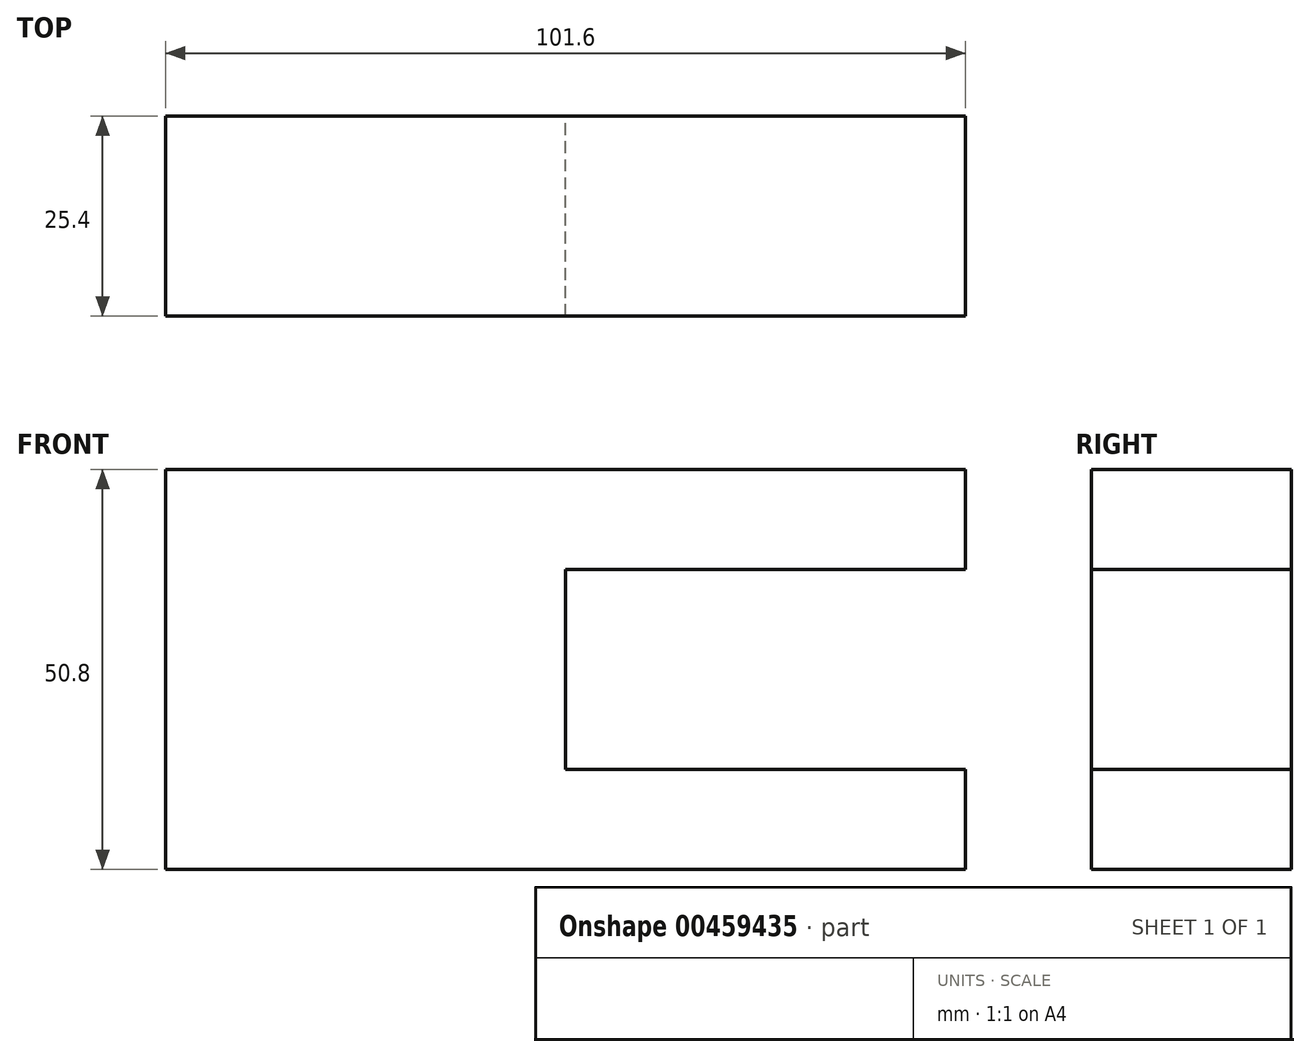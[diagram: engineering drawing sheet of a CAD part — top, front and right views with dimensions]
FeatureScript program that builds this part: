
annotation { "Feature Type Name" : "Feature", "Feature Type Description" : "" }
export const myFeature = defineFeature(function(context is Context, id is Id, definition is map)
    precondition{}
    {
        {
            var Q0;
            Q0=qCreatedBy(makeId("Front.planeOp"),FACE);
            var sketch = newSketch(context, id + "F0", { "sketchPlane" : qUnion([Q0])});
            skLineSegment(sketch, "E0.bottom", {"start": v(-50.8, -25.4) * mm, "end": v(50.8, -25.4) * mm});
            skLineSegment(sketch, "E0.top", {"start": v(-50.8, 25.4) * mm, "end": v(50.8, 25.4) * mm});
            skLineSegment(sketch, "E0.left", {"start": v(-50.8, -25.4) * mm, "end": v(-50.8, 25.4) * mm});
            skLineSegment(sketch, "E0.right", {"start": v(50.8, -25.4) * mm, "end": v(50.8, 25.4) * mm});
            skPoint(sketch, "E0.middle", {"position": v(0, 0) * mm});
            skSolve(sketch);
        }
        {
            var Q0;
            Q0=makeQuery(id+"F0.imprint","IMPRINT",FACE,{"disambiguationData":[TD([[makeQuery(id+"F0.imprint","IMPRINT",EDGE,{"derivedFrom":sQuery(id+"F0.wireOp",EDGE,"E0.bottom")}),1.0]])]});
            extrude(context, id + "F1", {"entities" : qUnion([Q0]), "depth" : 25.4 * mm});
        }
        {
            var Q0;
            Q0=qCreatedBy(makeId("Front.planeOp"),FACE);
            var sketch = newSketch(context, id + "F2", { "sketchPlane" : qUnion([Q0])});
            skLineSegment(sketch, "E1.bottom", {"start": v(50.8, 12.7) * mm, "end": v(0, 12.7) * mm});
            skLineSegment(sketch, "E1.top", {"start": v(50.8, -12.7) * mm, "end": v(0, -12.7) * mm});
            skLineSegment(sketch, "E1.left", {"start": v(50.8, 12.7) * mm, "end": v(50.8, -12.7) * mm});
            skLineSegment(sketch, "E1.right", {"start": v(0, 12.7) * mm, "end": v(0, -12.7) * mm});
            skSolve(sketch);
        }
        {
            var Q0;
            Q0 = qSketchRegion(id + "F2", true);
            extrude(context, id + "F3", {"entities" : qUnion([Q0]), "operationType" : NewBodyOperationType.REMOVE, "endBound" : BoundingType.THROUGH_ALL, "depth" : 25.4 * mm});
        }
    });
